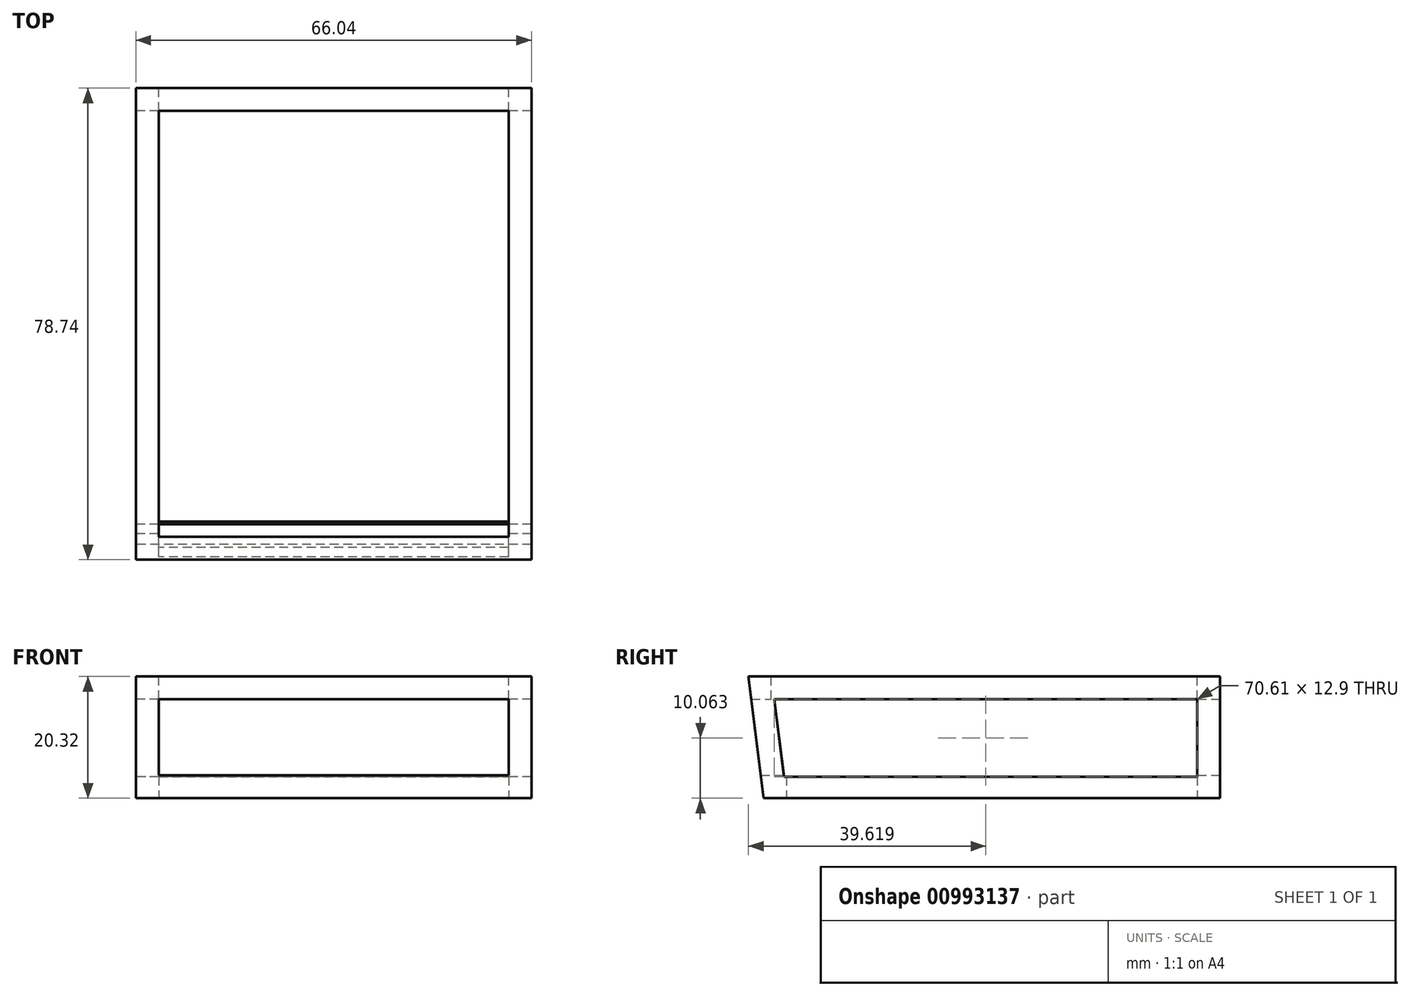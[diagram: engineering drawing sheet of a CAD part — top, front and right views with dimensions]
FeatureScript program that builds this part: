
annotation { "Feature Type Name" : "Feature", "Feature Type Description" : "" }
export const myFeature = defineFeature(function(context is Context, id is Id, definition is map)
    precondition{}
    {
        {
            var Q0;
            Q0=qCreatedBy(makeId("Right.planeOp"),FACE);
            var sketch = newSketch(context, id + "F0", { "sketchPlane" : qUnion([Q0])});
            skLineSegment(sketch, "E0", {"start": v(-77.21, 16.04) * mm, "end": v(-1.01, 16.04) * mm});
            skLineSegment(sketch, "E1", {"start": v(-1.01, 16.04) * mm, "end": v(-1.01, 36.36) * mm});
            skLineSegment(sketch, "E2", {"start": v(-1.01, 36.36) * mm, "end": v(-79.75, 36.36) * mm});
            skLineSegment(sketch, "E3", {"start": v(-79.75, 36.36) * mm, "end": v(-77.21, 16.04) * mm});
            skLineSegment(sketch, "E4.bottom", {"start": v(-4.82, 32.55) * mm, "end": v(-75.44, 32.55) * mm});
            skLineSegment(sketch, "E4.left", {"start": v(-4.82, 32.55) * mm, "end": v(-4.82, 19.65) * mm});
            skLineSegment(sketch, "E5", {"start": v(-75.44, 32.55) * mm, "end": v(-73.83, 19.65) * mm});
            skLineSegment(sketch, "E6", {"start": v(-73.83, 19.65) * mm, "end": v(-4.82, 19.65) * mm});
            skSolve(sketch);
        }
        {
            var Q0;
            Q0=makeQuery(id+"F0.imprint","IMPRINT",FACE,{"disambiguationData":[TD([[makeQuery(id+"F0.imprint","IMPRINT",EDGE,{"derivedFrom":sQuery(id+"F0.wireOp",EDGE,"E0")}),1.0]])]});
            extrude(context, id + "F1", {"entities" : qUnion([Q0]), "depth" : 66.04 * mm, "offsetDistance" : 25.4 * mm});
        }
        {
            var Q0;
            Q0=makeQuery(id+"F1.opExtrude","SWEPT_FACE",FACE,{"disambiguationData":[OSD([sQuery(id+"F0.wireOp",EDGE,"E2")])]});
            var sketch = newSketch(context, id + "F2", { "sketchPlane" : qUnion([Q0])});
            skLineSegment(sketch, "E7.bottom", {"start": v(3.8, -4.82) * mm, "end": v(62.23, -4.82) * mm});
            skLineSegment(sketch, "E7.top", {"start": v(3.81, -75.94) * mm, "end": v(62.23, -75.94) * mm});
            skLineSegment(sketch, "E7.left", {"start": v(3.81, -4.82) * mm, "end": v(3.81, -75.94) * mm});
            skLineSegment(sketch, "E7.right", {"start": v(62.23, -4.82) * mm, "end": v(62.23, -75.94) * mm});
            skSolve(sketch);
        }
        {
            var Q0;
            Q0=makeQuery(id+"F2.imprint","IMPRINT",FACE,{"disambiguationData":[TD([[makeQuery(id+"F2.imprint","IMPRINT",EDGE,{"derivedFrom":sQuery(id+"F2.wireOp",EDGE,"E7.bottom")}),-1.0]])]});
            extrude(context, id + "F3", {"entities" : qUnion([Q0]), "operationType" : NewBodyOperationType.REMOVE, "oppositeDirection" : true, "depth" : 3.8 * mm, "offsetDistance" : 25.4 * mm});
        }
        {
            var Q0;
            Q0=makeQuery(id+"F1.opExtrude","SWEPT_FACE",FACE,{"disambiguationData":[OSD([sQuery(id+"F0.wireOp",EDGE,"E1")])]});
            var sketch = newSketch(context, id + "F4", { "sketchPlane" : qUnion([Q0])});
            skLineSegment(sketch, "E8.bottom", {"start": v(-62.23, 32.55) * mm, "end": v(-3.81, 32.55) * mm});
            skLineSegment(sketch, "E8.top", {"start": v(-62.23, 19.85) * mm, "end": v(-3.81, 19.85) * mm});
            skLineSegment(sketch, "E8.left", {"start": v(-62.23, 32.55) * mm, "end": v(-62.23, 19.85) * mm});
            skLineSegment(sketch, "E8.right", {"start": v(-3.81, 32.55) * mm, "end": v(-3.8, 19.85) * mm});
            skSolve(sketch);
        }
        {
            var Q0;
            Q0=makeQuery(id+"F4.imprint","IMPRINT",FACE,{"disambiguationData":[TD([[makeQuery(id+"F4.imprint","IMPRINT",EDGE,{"derivedFrom":sQuery(id+"F4.wireOp",EDGE,"E8.bottom")}),-1.0]])]});
            extrude(context, id + "F5", {"entities" : qUnion([Q0]), "operationType" : NewBodyOperationType.REMOVE, "oppositeDirection" : true, "depth" : 101.6 * mm, "offsetDistance" : 25.4 * mm});
        }
        {
            var Q0;
            Q0=makeQuery(id+"F1.opExtrude","SWEPT_FACE",FACE,{"disambiguationData":[OSD([sQuery(id+"F0.wireOp",EDGE,"E0")])]});
            var sketch = newSketch(context, id + "F6", { "sketchPlane" : qUnion([Q0])});
            skLineSegment(sketch, "E9.bottom", {"start": v(62.23, 73.4) * mm, "end": v(3.8, 73.4) * mm});
            skLineSegment(sketch, "E9.top", {"start": v(62.23, 4.82) * mm, "end": v(3.81, 4.82) * mm});
            skLineSegment(sketch, "E9.left", {"start": v(62.23, 73.4) * mm, "end": v(62.23, 4.82) * mm});
            skLineSegment(sketch, "E9.right", {"start": v(3.8, 73.4) * mm, "end": v(3.81, 4.82) * mm});
            skSolve(sketch);
        }
        {
            var Q0;
            Q0=makeQuery(id+"F6.imprint","IMPRINT",FACE,{"disambiguationData":[TD([[makeQuery(id+"F6.imprint","IMPRINT",EDGE,{"derivedFrom":sQuery(id+"F6.wireOp",EDGE,"E9.bottom")}),1.0]])]});
            extrude(context, id + "F7", {"entities" : qUnion([Q0]), "operationType" : NewBodyOperationType.REMOVE, "oppositeDirection" : true, "depth" : 25.4 * mm, "offsetDistance" : 25.4 * mm});
        }
    });
